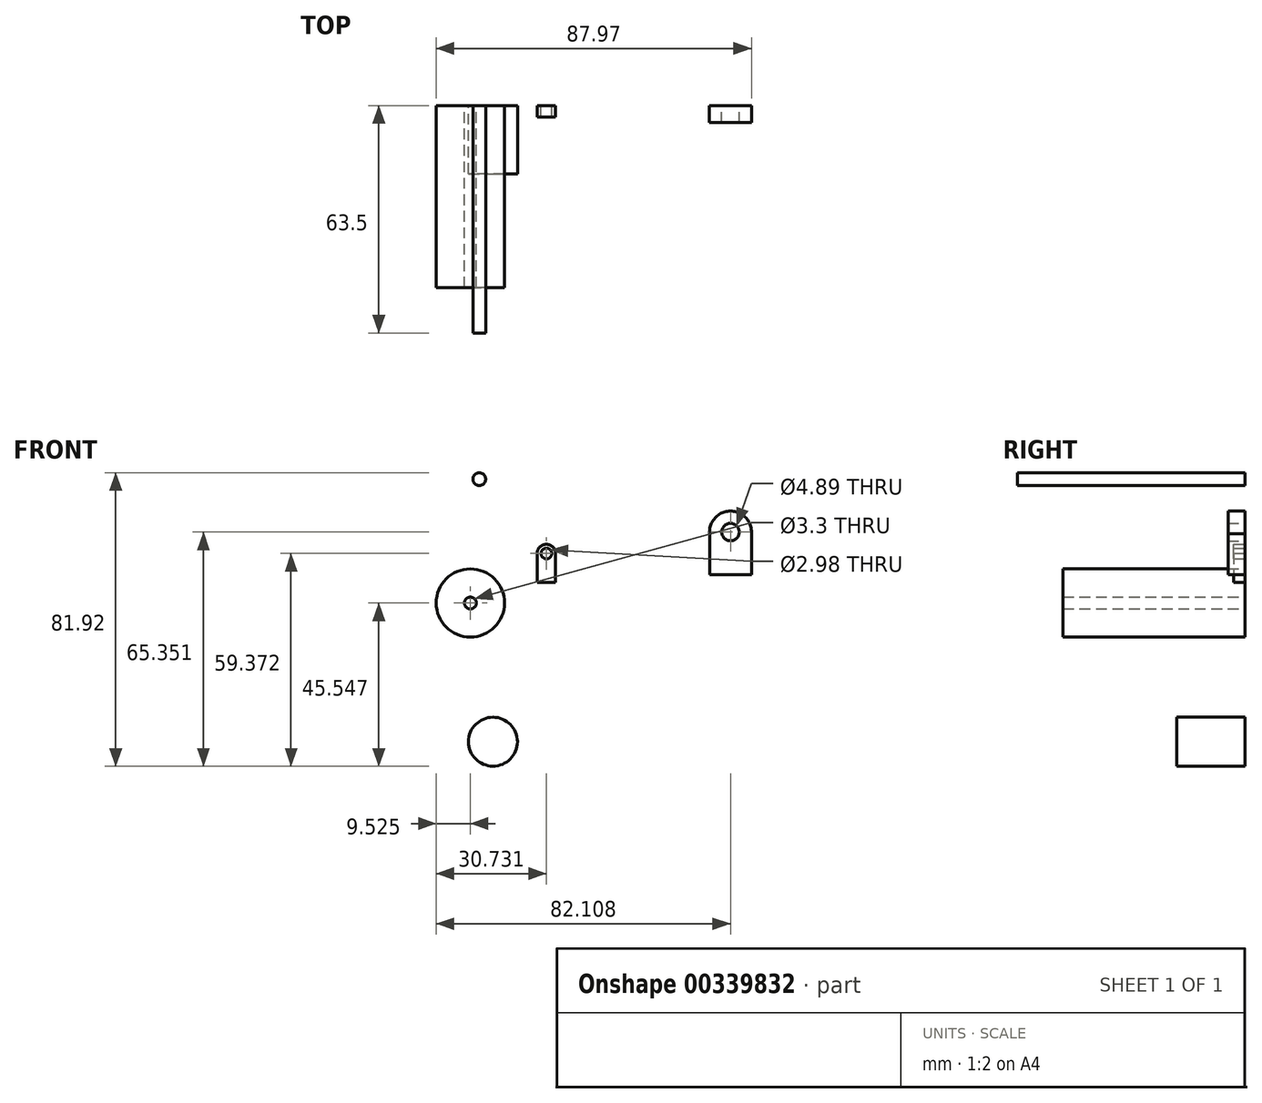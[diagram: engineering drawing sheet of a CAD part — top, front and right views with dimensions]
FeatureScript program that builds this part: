
annotation { "Feature Type Name" : "Feature", "Feature Type Description" : "" }
export const myFeature = defineFeature(function(context is Context, id is Id, definition is map)
    precondition{}
    {
        {
            var Q0;
            Q0=qCreatedBy(makeId("Front.planeOp"),FACE);
            var sketch = newSketch(context, id + "F0", { "sketchPlane" : qUnion([Q0])});
            skCircle(sketch, "E0", {"center": v(-41.99, 12.48) * mm, "radius": 9.53 * mm});
            skSolve(sketch);
        }
        {
            var Q0;
            Q0=makeQuery(id+"F0.imprint","IMPRINT",FACE,{"disambiguationData":[TD([[makeQuery(id+"F0.imprint","IMPRINT",EDGE,{"derivedFrom":sQuery(id+"F0.wireOp",EDGE,"E0")}),1.0]])]});
            extrude(context, id + "F1", {"entities" : qUnion([Q0]), "depth" : 50.8 * mm});
        }
        {
            var Q0;
            Q0=makeQuery(id+"F1.opExtrude","CAP_FACE",FACE,{"disambiguationData":[OSD([sQuery(id+"F0.wireOp",EDGE,"E0")])],"isStart":false});
            var sketch = newSketch(context, id + "F2", { "sketchPlane" : qUnion([Q0])});
            skCircle(sketch, "E1", {"center": v(-41.99, 12.48) * mm, "radius": 5.4 * mm});
            skSolve(sketch);
        }
        {
            var Q0;
            Q0=sQuery(id+"F2.wireOp",VERTEX,"E1.center");
            var Q1;
            Q1=makeQuery(id+"F1.opExtrude","SWEPT_BODY",BODY,{"disambiguationData":[OSD([sQuery(id+"F0.wireOp",EDGE,"E0")])]});
            hole(context, id + "F3", {"style" : HoleStyle.SIMPLE, "endStyle" : HoleEndStyle.THROUGH, "standardTappedOrClearance" : lookupTablePath({ "standard" : "ISO", "fit" : "Normal", "size" : "M3", "type" : "Clearance" }), "standardBlindInLast" : lookupTablePath({ "fit" : "Standard", "standard" : "ISO", "size" : "M3", "type" : "Clearance" }), "holeDiameter" : 3.3 * mm, "isTappedThrough" : true, "tappedDepth" : 12.7 * mm, "tapClearance" : 3, "locations" : qUnion([Q0]), "scope" : qUnion([Q1]), "startStyle" : HoleStartStyle.PART});
        }
        {
            var Q0;
            Q0=qCreatedBy(makeId("Front.planeOp"),FACE);
            var sketch = newSketch(context, id + "F4", { "sketchPlane" : qUnion([Q0])});
            skCircle(sketch, "E2", {"center": v(-39.51, 47.06) * mm, "radius": 1.79 * mm});
            skSolve(sketch);
        }
        {
            var Q0;
            Q0=makeQuery(id+"F4.imprint","IMPRINT",FACE,{"disambiguationData":[TD([[makeQuery(id+"F4.imprint","IMPRINT",EDGE,{"derivedFrom":sQuery(id+"F4.wireOp",EDGE,"E2")}),1.0]])]});
            extrude(context, id + "F5", {"entities" : qUnion([Q0]), "depth" : 63.5 * mm});
        }
        {
            var Q0;
            Q0=qCreatedBy(makeId("Front.planeOp"),FACE);
            var sketch = newSketch(context, id + "F6", { "sketchPlane" : qUnion([Q0])});
            skCircle(sketch, "E3", {"center": v(-35.68, -26.24) * mm, "radius": 6.83 * mm});
            skSolve(sketch);
        }
        {
            var Q0;
            Q0=makeQuery(id+"F6.imprint","IMPRINT",FACE,{"disambiguationData":[TD([[makeQuery(id+"F6.imprint","IMPRINT",EDGE,{"derivedFrom":sQuery(id+"F6.wireOp",EDGE,"E3")}),1.0]])]});
            extrude(context, id + "F7", {"entities" : qUnion([Q0]), "depth" : 19.05 * mm});
        }
        {
            var Q0;
            Q0=qCreatedBy(makeId("Front.planeOp"),FACE);
            var sketch = newSketch(context, id + "F8", { "sketchPlane" : qUnion([Q0])});
            skLineSegment(sketch, "E4.top", {"start": v(24.76, 20.4) * mm, "end": v(36.44, 20.4) * mm});
            skLineSegment(sketch, "E4.left", {"start": v(24.76, 32.28) * mm, "end": v(24.76, 20.4) * mm});
            skLineSegment(sketch, "E4.right", {"start": v(36.44, 32.28) * mm, "end": v(36.44, 20.4) * mm});
            skArc(sketch, "E5", {"start": v(36.44, 31.79) * mm, "mid": v(30.6, 38.14) * mm, "end": v(24.76, 31.79) * mm});
            skCircle(sketch, "E6", {"center": v(30.6, 32.28) * mm, "radius": 2.45 * mm});
            skSolve(sketch);
        }
        {
            var Q0;
            {var subQ2=sQuery(id+"F8.wireOp",EDGE,"E4.top");Q0=makeQuery(id+"F8.imprint","IMPRINT",FACE,{"disambiguationData":[TD([[makeQuery(id+"F8.imprint","IMPRINT",EDGE,{"derivedFrom":subQ2}),1.0]])]});}
            extrude(context, id + "F9", {"entities" : qUnion([Q0]), "depth" : 4.75 * mm});
        }
        {
            var Q0;
            Q0=qCreatedBy(makeId("Front.planeOp"),FACE);
            var sketch = newSketch(context, id + "F10", { "sketchPlane" : qUnion([Q0])});
            skLineSegment(sketch, "E7.bottom", {"start": v(-23.36, 26.3) * mm, "end": v(-23.36, 26.3) * mm});
            skLineSegment(sketch, "E7.top", {"start": v(-23.36, 18.29) * mm, "end": v(-18.2, 18.29) * mm});
            skLineSegment(sketch, "E7.left", {"start": v(-23.36, 26.3) * mm, "end": v(-23.36, 18.29) * mm});
            skLineSegment(sketch, "E7.right", {"start": v(-18.2, 26.3) * mm, "end": v(-18.2, 18.29) * mm});
            skArc(sketch, "E8", {"start": v(-18.2, 26.3) * mm, "mid": v(-20.78, 28.88) * mm, "end": v(-23.36, 26.3) * mm});
            skLineSegment(sketch, "E9.trimOffspring", {"start": v(-18.2, 26.3) * mm, "end": v(-18.2, 26.3) * mm});
            skCircle(sketch, "E10", {"center": v(-20.78, 26.3) * mm, "radius": 1.5 * mm});
            skSolve(sketch);
        }
        {
            var Q0;
            Q0=makeQuery(id+"F10.imprint","IMPRINT",FACE,{"disambiguationData":[TD([[makeQuery(id+"F10.imprint","IMPRINT",EDGE,{"derivedFrom":sQuery(id+"F10.wireOp",EDGE,"E7.bottom")}),-1.0]])]});
            extrude(context, id + "F11", {"entities" : qUnion([Q0]), "depth" : 3.17 * mm});
        }
    });
